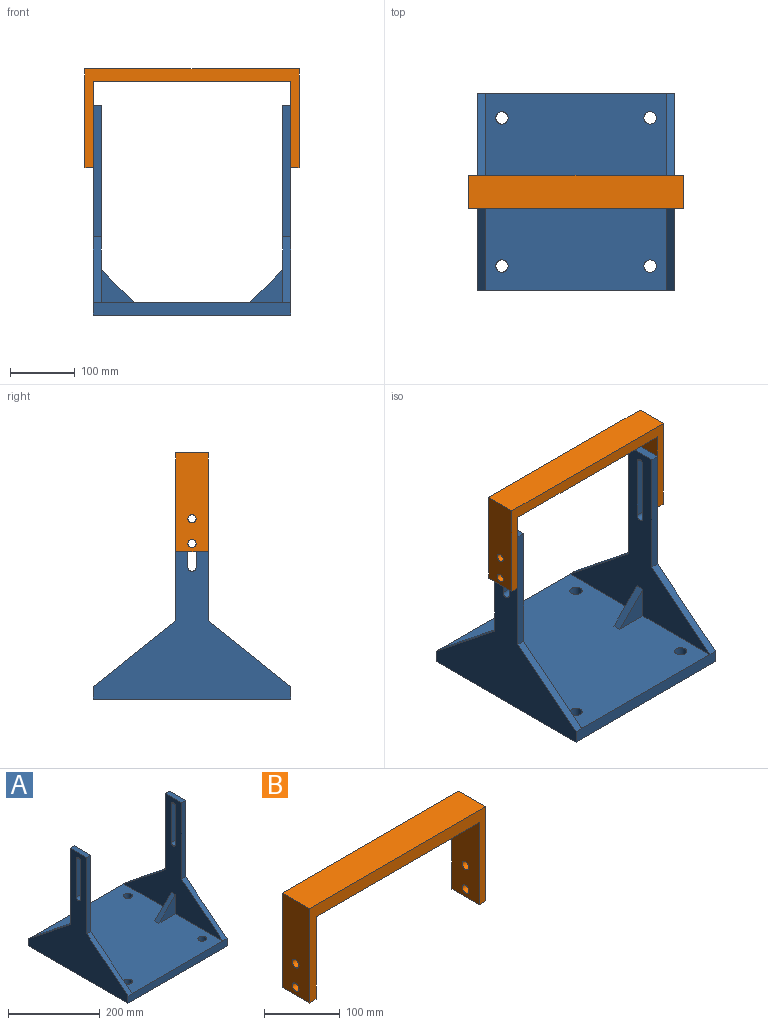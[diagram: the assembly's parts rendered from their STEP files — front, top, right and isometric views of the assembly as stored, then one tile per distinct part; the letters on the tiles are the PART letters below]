
ASSEMBLY  parts=2 mates=2
PART A: 36 faces, bbox 304.8x304.8x323.9 mm
  f0: plane 304.8x279.4mm, normal (0,0,1), area 82730.7mm2, adj f3,f6,f7,f9,f17,f18,f19,f27
  f1: plane 203.2x12.7mm, normal (0,1,0), area 2580.6mm2, adj f3,f10,f22,f31
  f2: plane 203.2x12.7mm, normal (0,-1,0), area 2580.6mm2, adj f3,f10,f22,f30
  f3: plane 304.8x304.8mm, normal (1,0,0), area 26324.9mm2, adj f0,f1,f2,f22,f23,f24,f25,f26
  f4: plane 203.2x12.7mm, normal (0,1,0), area 2580.6mm2, adj f6,f8,f12,f21
  f5: plane 203.2x12.7mm, normal (0,-1,0), area 2580.6mm2, adj f6,f8,f12,f20
  f6: plane 304.8x304.8mm, normal (-1,0,0), area 26324.9mm2, adj f0,f4,f5,f12,f13,f14,f15,f16
  f7: plane 304.8x19.05mm, normal (0,-1,0), area 5806.4mm2, adj f0,f8,f10,f11,f20,f30
  f8: plane 323.85x304.8mm, normal (1,0,0), area 32776.5mm2, adj f4,f5,f7,f9,f11,f12,f13,f14
  f9: plane 304.8x19.05mm, normal (0,1,0), area 5806.4mm2, adj f0,f8,f10,f11,f21,f31
  f10: plane 323.85x304.8mm, normal (-1,0,0), area 32776.5mm2, adj f1,f2,f7,f9,f11,f22,f23,f24
  f11: plane 304.8x304.8mm, normal (0,0,-1), area 91762.9mm2, adj f7,f8,f9,f10,f32,f33,f34,f35
  f12: plane 50.8x12.7mm, normal (0,0,1), area 645.2mm2, adj f4,f5,f6,f8
  f13: plane 101.6x12.7mm, normal (0,1,0), area 1290.3mm2, adj f6,f8,f14,f16
  f14: cylinder r=6.35mm len=12.7mm, axis (1,0,0), area 253.4mm2, adj f6,f8,f13,f15
  f15: plane 101.6x12.7mm, normal (0,-1,0), area 1290.3mm2, adj f6,f8,f14,f16
  f16: cylinder r=6.35mm len=12.7mm, axis (1,0,0), area 253.4mm2, adj f6,f8,f13,f15
  f17: plane 50.8x50.8mm, normal (-0.71,0,0.71), area 912.4mm2, adj f0,f6,f18,f19
  f18: plane 50.8x50.8mm, normal (0,-1,0), area 1290.3mm2, adj f0,f6,f17
  f19: plane 50.8x50.8mm, normal (0,1,0), area 1290.3mm2, adj f0,f6,f17
  f20: plane 127x101.6mm, normal (0,-0.62,0.78), area 2065.5mm2, adj f5,f6,f7,f8
  f21: plane 127x101.6mm, normal (0,0.62,0.78), area 2065.5mm2, adj f4,f6,f8,f9
  f22: plane 50.8x12.7mm, normal (0,0,1), area 645.2mm2, adj f1,f2,f3,f10
  f23: plane 101.6x12.7mm, normal (0,1,0), area 1290.3mm2, adj f3,f10,f24,f26
  f24: cylinder r=6.35mm len=12.7mm, axis (-1,0,0), area 253.4mm2, adj f3,f10,f23,f25
  f25: plane 101.6x12.7mm, normal (0,-1,0), area 1290.3mm2, adj f3,f10,f24,f26
  f26: cylinder r=6.35mm len=12.7mm, axis (-1,0,0), area 253.4mm2, adj f3,f10,f23,f25
  f27: plane 50.8x50.8mm, normal (0.71,0,0.71), area 912.4mm2, adj f0,f3,f28,f29
  f28: plane 50.8x50.8mm, normal (0,-1,0), area 1290.3mm2, adj f0,f3,f27
  f29: plane 50.8x50.8mm, normal (0,1,0), area 1290.3mm2, adj f0,f3,f27
  f30: plane 127x101.6mm, normal (0,-0.62,0.78), area 2065.5mm2, adj f2,f3,f7,f10
  f31: plane 127x101.6mm, normal (0,0.62,0.78), area 2065.5mm2, adj f1,f3,f9,f10
  f32: cylinder r=9.53mm len=19.05mm, axis (0,0,1), area 1140.1mm2, adj f0,f11
  f33: cylinder r=9.53mm len=19.05mm, axis (0,0,1), area 1140.1mm2, adj f0,f11
  f34: cylinder r=9.53mm len=19.05mm, axis (0,0,1), area 1140.1mm2, adj f0,f11
  f35: cylinder r=9.53mm len=19.05mm, axis (0,0,1), area 1140.1mm2, adj f0,f11
PART B: 14 faces, bbox 330.2x50.8x152.4 mm
  f0: plane 330.2x152.4mm, normal (0,-1,0), area 9677.4mm2, adj f2,f3,f4,f5,f6,f9,f10,f11
  f1: plane 330.2x152.4mm, normal (0,1,0), area 9677.4mm2, adj f2,f3,f4,f5,f6,f9,f10,f11
  f2: plane 330.2x50.8mm, normal (0,0,1), area 16774.2mm2, adj f0,f1,f5,f11
  f3: plane 304.8x50.8mm, normal (0,0,-1), area 15483.8mm2, adj f0,f1,f6,f9
  f4: plane 50.8x12.7mm, normal (0,0,-1), area 645.2mm2, adj f0,f1,f5,f6
  f5: plane 152.4x50.8mm, normal (1,0,0), area 7488.6mm2, adj f0,f1,f2,f4,f7,f8
  f6: plane 133.35x50.8mm, normal (-1,0,0), area 6520.8mm2, adj f0,f1,f3,f4,f7,f8
  f7: cylinder r=6.35mm len=12.7mm, axis (1,0,0), area 506.7mm2, adj f5,f6
  f8: cylinder r=6.35mm len=12.7mm, axis (1,0,0), area 506.7mm2, adj f5,f6
  f9: plane 133.35x50.8mm, normal (1,0,0), area 6520.8mm2, adj f0,f1,f3,f10,f12,f13
  f10: plane 50.8x12.7mm, normal (0,0,-1), area 645.2mm2, adj f0,f1,f9,f11
  f11: plane 152.4x50.8mm, normal (-1,0,0), area 7488.6mm2, adj f0,f1,f2,f10,f12,f13
  f12: cylinder r=6.35mm len=12.7mm, axis (-1,0,0), area 506.7mm2, adj f9,f11
  f13: cylinder r=6.35mm len=12.7mm, axis (-1,0,0), area 506.7mm2, adj f9,f11
PLACE A t=(-141.3,15.55,-16.23)mm fixed
PLACE B t=(-141.3,15.55,344.37)mm
MATE planar B.f0 <-> A.f2  axis (0,-1,0) through (-141.3,-9.85,327.22)mm
MATE planar B.f9 <-> A.f10  axis (1,0,0) through (-293.7,15.55,279.05)mm
